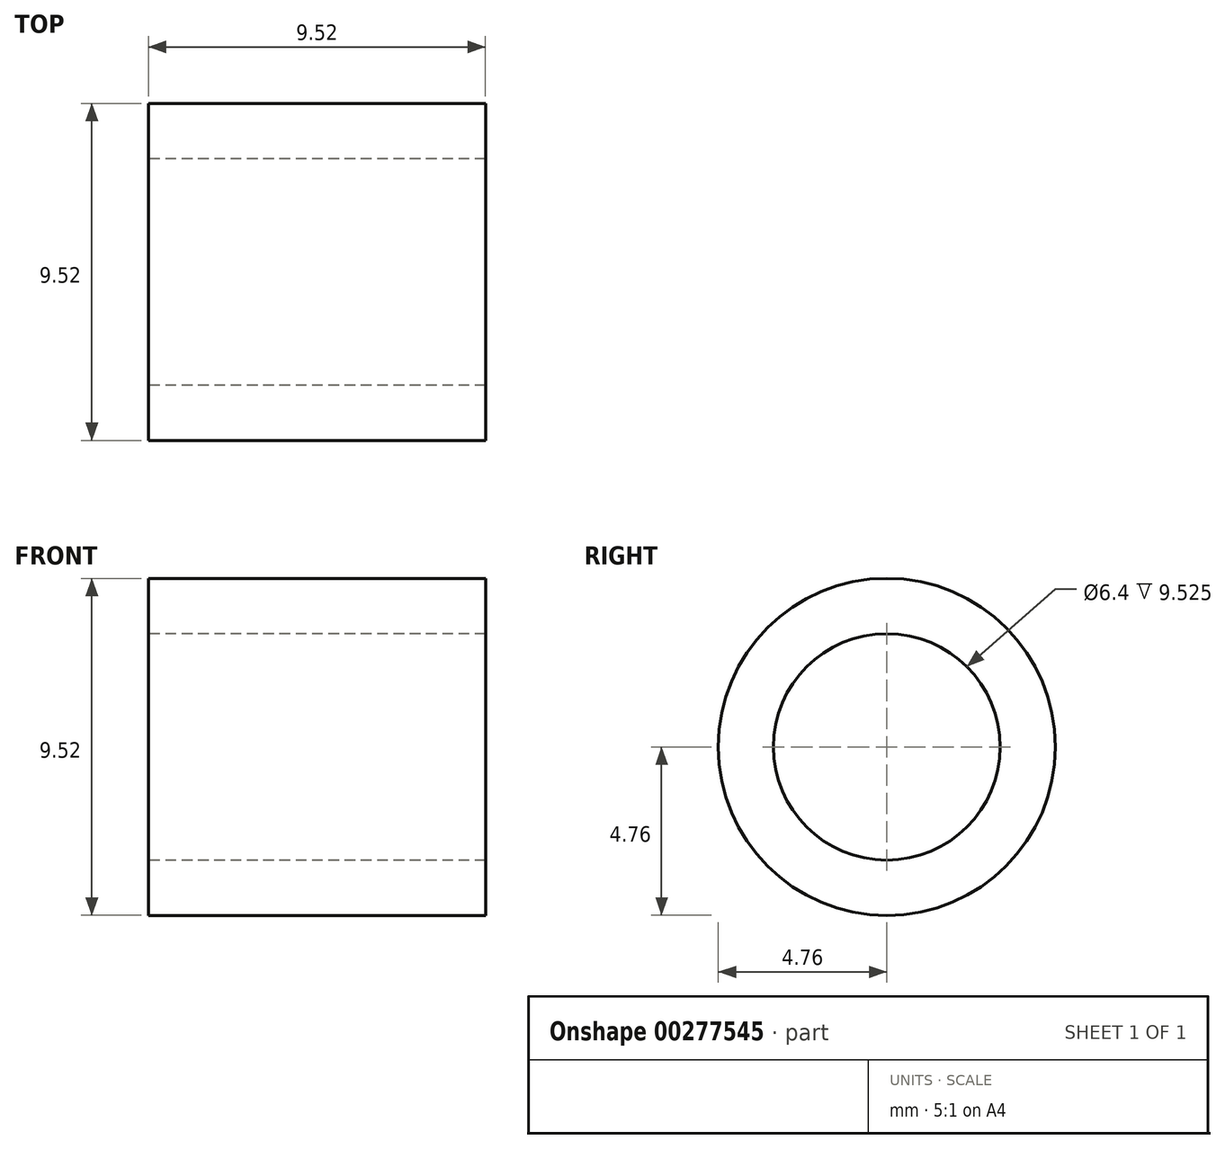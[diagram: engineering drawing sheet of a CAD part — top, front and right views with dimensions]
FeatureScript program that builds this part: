
annotation { "Feature Type Name" : "Feature", "Feature Type Description" : "" }
export const myFeature = defineFeature(function(context is Context, id is Id, definition is map)
    precondition{}
    {
        {
            var Q0;
            Q0=qCreatedBy(makeId("Right.planeOp"),FACE);
            var sketch = newSketch(context, id + "F0", { "sketchPlane" : qUnion([Q0])});
            skCircle(sketch, "E0", {"center": v(0, 0) * mm, "radius": 4.76 * mm});
            skCircle(sketch, "E1", {"center": v(0, 0) * mm, "radius": 3.2 * mm});
            skSolve(sketch);
        }
        {
            var Q0;
            Q0 = qSketchRegion(id + "F0", true);
            extrude(context, id + "F1", {"entities" : qUnion([Q0]), "endBound" : BoundingType.SYMMETRIC, "depth" : 9.52 * mm});
        }
    });
